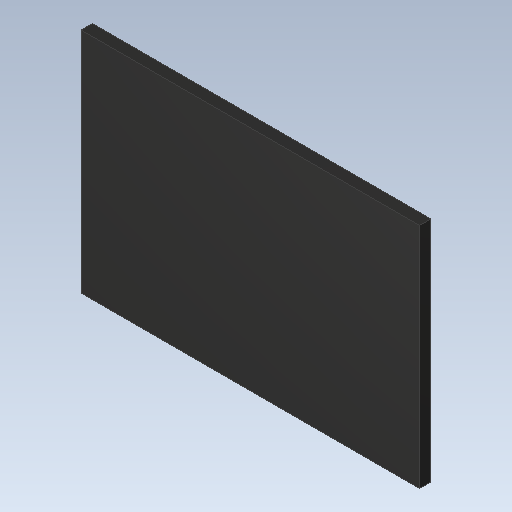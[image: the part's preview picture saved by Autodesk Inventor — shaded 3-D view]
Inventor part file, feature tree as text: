
AUTODESK INVENTOR PART (.ipt)
format: ipt  version: 2020 (Build 240168000, 168)  size: 87,040 bytes
history: imported  units: in
note: dims shown in document units (in); Inventor stores cm internally (conversion verified against a paired STEP export)
features: imported_body x1
ambient origin geometry x8: Origin, YZ Plane, XZ Plane, XY Plane, X Axis, Y Axis, Z Axis, Center Point
bodies: Solid1 (imported_parasolid), Body1 (imported_parasolid)
feature tree (1):
  imported_body  NMx_Import_Brep_tag  [imported B-rep: ~6 faces, bbox_mm=[2.9968, 2.0168, 0.1]]
